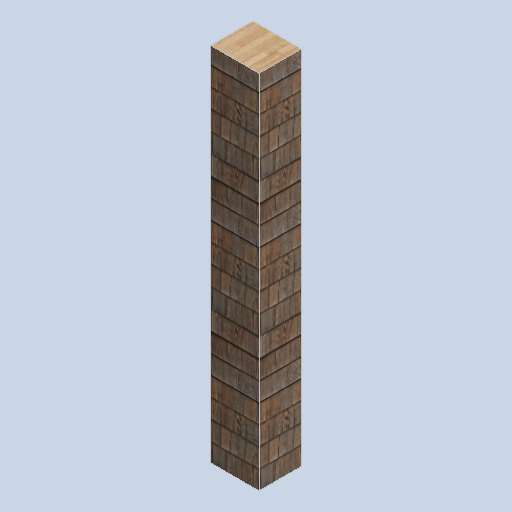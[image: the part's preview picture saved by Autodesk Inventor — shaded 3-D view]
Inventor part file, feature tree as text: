
AUTODESK INVENTOR PART (.ipt)
format: ipt  version: 2024.2 (Build 282272000, 272)  size: 359,936 bytes
history: native  units: mm
features: extrude x1, sketch x1
ambient origin geometry x8: Origin, YZ Plane, XZ Plane, XY Plane, X Axis, Y Axis, Z Axis, Center Point
bodies: Solid1 (feature_tree)
feature tree (2):
  extrude  "Extrusion1"  Depth=350.0mm
  sketch  "Sketch1"  dims[d0=400.0mm d1=350.0mm d2=3000.0mm d3=0.0mm]
